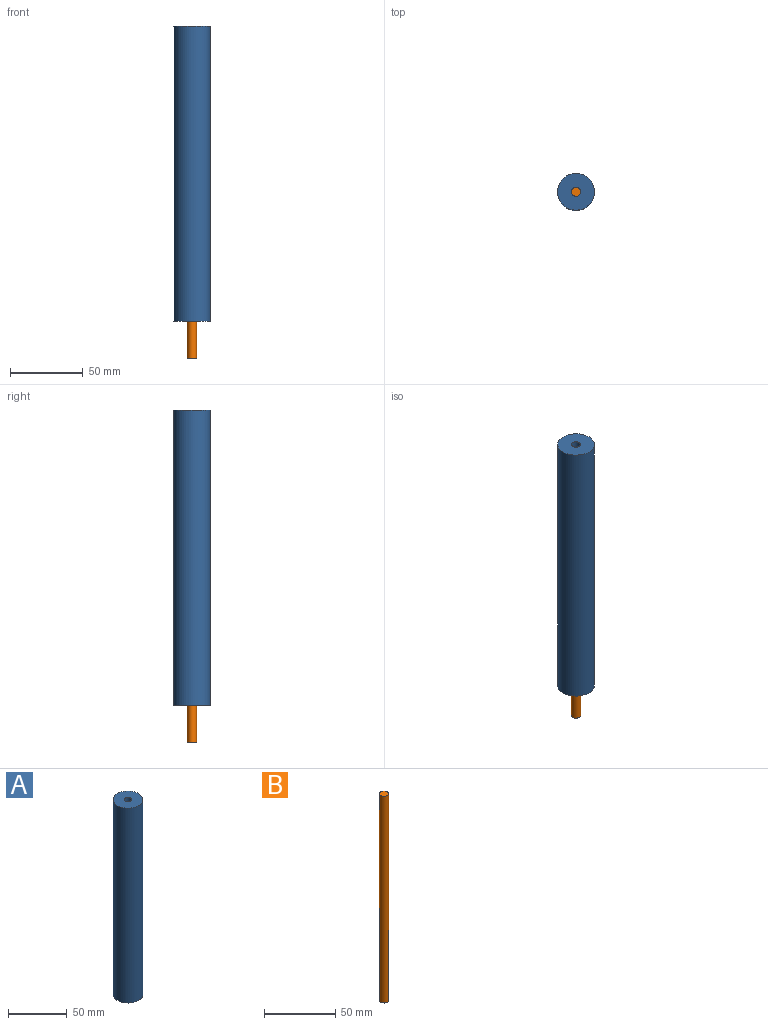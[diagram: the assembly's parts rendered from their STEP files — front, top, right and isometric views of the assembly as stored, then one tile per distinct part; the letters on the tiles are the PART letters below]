
ASSEMBLY  parts=2 mates=1
PART A: 4 faces, bbox 25.4x25.4x203.2 mm
  f0: cylinder r=3.17mm len=203.2mm, axis (0,0,-1), area 4053.7mm2, adj f2,f3
  f1: cylinder r=12.7mm len=203.2mm, axis (0,0,-1), area 16214.6mm2, adj f2,f3
  f2: plane 25.4x25.4mm, normal (0,0,1), area 475mm2, adj f0,f1
  f3: plane 25.4x25.4mm, normal (0,0,-1), area 475mm2, adj f0,f1
PART B: 3 faces, bbox 6.4x6.4x177.8 mm
  f0: cylinder r=3.17mm len=177.8mm, axis (0,0,1), area 3547mm2, adj f1,f2
  f1: plane 6.35x6.35mm, normal (0,0,-1), area 31.7mm2, adj f0
  f2: plane 6.35x6.35mm, normal (0,0,1), area 31.7mm2, adj f0
PLACE A t=(88.39,0,0)mm fixed
PLACE B rot(axis=(0,0,-1),6.8deg) t=(82.53,-13.68,152.4)mm
MATE cylindrical A.f0 <-> B.f0  axis (0,0,-1) through (-30.13,42.72,0)mm
